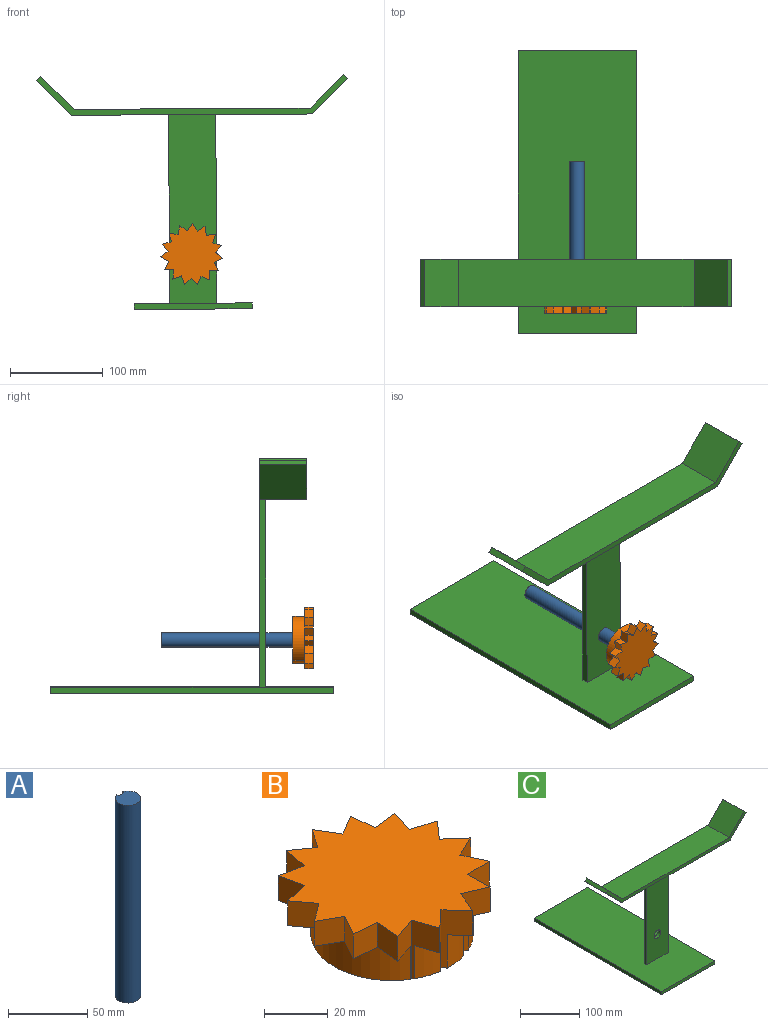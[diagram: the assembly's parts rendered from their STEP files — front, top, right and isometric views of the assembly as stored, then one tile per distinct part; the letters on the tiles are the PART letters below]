
ASSEMBLY  parts=3 mates=2
PART A: 6 faces, bbox 15.9x15.5x152.4 mm
  f0: plane 152.4x4.76mm, normal (0,1,0), area 725.8mm2, adj f1,f3,f4,f5
  f1: plane 152.4x1.59mm, normal (1,0,0), area 241.9mm2, adj f0,f2,f4,f5
  f2: cylinder r=7.94mm len=152.4mm, axis (0,0,-1), area 6863.5mm2, adj f1,f3,f4,f5
  f3: plane 152.4x1.59mm, normal (-1,0,0), area 241.9mm2, adj f0,f2,f4,f5
  f4: plane 15.88x15.51mm, normal (0,0,1), area 189.2mm2, adj f0,f1,f2,f3
  f5: plane 15.88x15.51mm, normal (0,0,-1), area 189.2mm2, adj f0,f1,f2,f3
PART B: 49 faces, bbox 66.6x66.5x22.2 mm
  f0: cylinder r=25.4mm len=50.45mm, axis (0,0,-1), area 1286.4mm2, adj f15,f16,f25,f36
  f1: cylinder r=25.4mm len=12.7mm, axis (0,0,-1), area 117.7mm2, adj f5,f15,f26,f27
  f2: cylinder r=25.4mm len=12.7mm, axis (0,0,-1), area 106.1mm2, adj f6,f15,f28,f29
  f3: cylinder r=25.4mm len=12.7mm, axis (0,0,-1), area 102mm2, adj f7,f15,f30,f31
  f4: cylinder r=25.4mm len=12.7mm, axis (0,0,-1), area 106.1mm2, adj f8,f15,f32,f33
  f5: plane 8.74x8.39mm, normal (0,0,-1), area 29.8mm2, adj f1,f26,f27
  f6: plane 8.25x6.82mm, normal (0,0,-1), area 24.7mm2, adj f2,f28,f29
  f7: plane 7.34x6.74mm, normal (0,0,-1), area 22.9mm2, adj f3,f30,f31
  f8: plane 7.42x7.21mm, normal (0,0,-1), area 24.7mm2, adj f4,f32,f33
  f9: plane 9.2x7.28mm, normal (0,0,-1), area 29.8mm2, adj f14,f34,f35
  f10: plane 12.7x1.59mm, normal (-1,0,0), area 20.2mm2, adj f11,f13,f15,f17
  f11: plane 12.7x4.76mm, normal (0,-1,0), area 60.5mm2, adj f10,f12,f15,f17
  f12: plane 12.7x1.59mm, normal (1,0,0), area 20.2mm2, adj f11,f13,f15,f17
  f13: cylinder r=7.94mm len=15.88mm, axis (0,0,-1), area 572mm2, adj f10,f12,f15,f17
  f14: cylinder r=25.4mm len=12.7mm, axis (0,0,-1), area 117.7mm2, adj f9,f15,f34,f35
  f15: plane 50.8x50.8mm, normal (0,0,-1), area 1826.6mm2, adj f0,f1,f2,f3,f4,f10,f11,f12
  f16: plane 65.64x59.76mm, normal (0,0,-1), area 545.8mm2, adj f0,f18,f19,f20,f21,f22,f23,f24
  f17: plane 15.88x15.51mm, normal (0,0,-1), area 189.2mm2, adj f10,f11,f12,f13
  f18: plane 9.6x9.53mm, normal (-0.22,0.98,0), area 93.8mm2, adj f16,f19,f44,f48
  f19: plane 9.53x7.89mm, normal (-0.8,-0.6,0), area 93.8mm2, adj f16,f18,f20,f48
  f20: plane 9.53x7.89mm, normal (-0.6,0.8,0), area 93.8mm2, adj f16,f19,f21,f48
  f21: plane 9.53x8.59mm, normal (-0.49,-0.87,0), area 93.8mm2, adj f16,f20,f22,f48
  f22: plane 9.53x8.59mm, normal (-0.87,0.49,0), area 93.8mm2, adj f16,f21,f23,f48
  f23: plane 9.8x9.53mm, normal (-0.09,-1,0), area 93.8mm2, adj f16,f22,f24,f48
  f24: plane 9.8x9.53mm, normal (-1,0.09,0), area 93.8mm2, adj f16,f23,f25,f48
  f25: plane 22.23x9.32mm, normal (0.32,-0.95,0), area 104.6mm2, adj f0,f15,f16,f24,f26,f48
  f26: plane 22.23x9.32mm, normal (-0.95,-0.32,0), area 106.4mm2, adj f1,f5,f15,f25,f27,f48
  f27: plane 22.23x7.23mm, normal (0.68,-0.73,0), area 117mm2, adj f1,f5,f15,f26,f28,f48
  f28: plane 22.23x7.23mm, normal (-0.73,-0.68,0), area 119.4mm2, adj f2,f6,f15,f27,f29,f48
  f29: plane 22.23x9.05mm, normal (0.92,-0.39,0), area 124.5mm2, adj f2,f6,f15,f28,f30,f48
  f30: plane 22.23x9.05mm, normal (-0.39,-0.92,0), area 125.6mm2, adj f3,f7,f15,f29,f31,f48
  f31: plane 22.23x9.85mm, normal (1,0.01,0), area 125.6mm2, adj f3,f7,f15,f30,f32,f48
  f32: plane 22.23x9.85mm, normal (0.01,-1,0), area 124.5mm2, adj f4,f8,f15,f31,f33,f48
  f33: plane 22.23x8.94mm, normal (0.91,0.42,0), area 119.4mm2, adj f4,f8,f15,f32,f34,f48
  f34: plane 22.23x8.94mm, normal (0.42,-0.91,0), area 117mm2, adj f9,f14,f15,f33,f35,f48
  f35: plane 22.23x7.4mm, normal (0.66,0.75,0), area 106.4mm2, adj f9,f14,f15,f34,f36,f48
  f36: plane 22.23x7.4mm, normal (0.75,-0.66,0), area 104.6mm2, adj f0,f15,f16,f35,f37,f48
  f37: plane 9.53x9.4mm, normal (0.3,0.96,0), area 93.8mm2, adj f16,f36,f38,f48
  f38: plane 9.53x9.4mm, normal (0.96,-0.3,0), area 93.8mm2, adj f16,f37,f39,f48
  f39: plane 9.78x9.53mm, normal (-0.12,0.99,0), area 93.8mm2, adj f16,f38,f40,f48
  f40: plane 9.78x9.53mm, normal (0.99,0.12,0), area 93.8mm2, adj f16,f39,f41,f48
  f41: plane 9.53x8.46mm, normal (-0.51,0.86,0), area 93.8mm2, adj f16,f40,f42,f48
  f42: plane 9.53x8.46mm, normal (0.86,0.51,0), area 93.8mm2, adj f16,f41,f43,f48
  f43: plane 9.53x8.04mm, normal (-0.82,0.58,0), area 93.8mm2, adj f16,f42,f45,f48
  f44: plane 9.6x9.53mm, normal (-0.98,-0.22,0), area 93.8mm2, adj f16,f18,f47,f48
  f45: plane 9.53x8.04mm, normal (0.58,0.82,0), area 93.8mm2, adj f16,f43,f46,f48
  f46: plane 9.66x9.53mm, normal (-0.98,0.2,0), area 93.8mm2, adj f16,f45,f47,f48
  f47: plane 9.66x9.53mm, normal (0.2,0.98,0), area 93.8mm2, adj f16,f44,f46,f48
  f48: plane 66.55x66.46mm, normal (0,0,1), area 2693.6mm2, adj f18,f19,f20,f21,f22,f23,f24,f25
PART C: 20 faces, bbox 334.8x304.8x251.8 mm
  f0: plane 304.8x127mm, normal (0,0,1), area 38387mm2, adj f1,f2,f3,f4,f6,f7,f8,f9
  f1: plane 127x6.35mm, normal (0,1,0), area 806.5mm2, adj f0,f2,f4,f5
  f2: plane 304.8x6.35mm, normal (-1,0,0), area 1935.5mm2, adj f0,f1,f3,f5
  f3: plane 127x6.35mm, normal (0,-1,0), area 806.5mm2, adj f0,f2,f4,f5
  f4: plane 304.8x6.35mm, normal (1,0,0), area 1935.5mm2, adj f0,f1,f3,f5
  f5: plane 304.8x127mm, normal (0,0,-1), area 38709.6mm2, adj f1,f2,f3,f4
  f6: plane 334.82x245.47mm, normal (0,1,0), area 12416.1mm2, adj f0,f7,f9,f10,f11,f12,f13,f14
  f7: plane 203.2x6.35mm, normal (-1,0,0), area 1290.3mm2, adj f0,f6,f8,f11
  f8: plane 203.2x50.8mm, normal (0,-1,0), area 10124.6mm2, adj f0,f7,f9,f10,f11
  f9: plane 203.2x6.35mm, normal (1,0,0), area 1290.3mm2, adj f0,f6,f8,f11
  f10: cylinder r=7.94mm len=15.88mm, axis (0,-1,0), area 316.7mm2, adj f6,f8
  f11: plane 259.26x50.8mm, normal (0,0,-1), area 12847.9mm2, adj f6,f7,f8,f9,f12,f18,f19
  f12: plane 50.8x37.78mm, normal (-0.71,0,-0.71), area 2714.3mm2, adj f6,f11,f13,f19
  f13: plane 50.8x4.49mm, normal (-0.71,0,0.71), area 322.6mm2, adj f6,f12,f14,f19
  f14: plane 50.8x35.92mm, normal (0.71,0,0.71), area 2580.6mm2, adj f6,f13,f15,f19
  f15: plane 254x50.8mm, normal (0,0,1), area 12903.2mm2, adj f6,f14,f16,f19
  f16: plane 50.8x35.92mm, normal (-0.71,0,0.71), area 2580.6mm2, adj f6,f15,f17,f19
  f17: plane 50.8x4.49mm, normal (0.71,0,0.71), area 322.6mm2, adj f6,f16,f18,f19
  f18: plane 50.8x37.78mm, normal (0.71,0,-0.71), area 2714.3mm2, adj f6,f11,f17,f19
  f19: plane 334.82x42.27mm, normal (0,-1,0), area 2291.5mm2, adj f11,f12,f13,f14,f15,f16,f17,f18
PLACE A rot(axis=(-0.98,0.13,0.13),91deg) t=(-19.15,32.01,51.47)mm
PLACE B rot(axis=(1,-0.01,0.01),90deg) t=(-19.15,30.39,51.47)mm
PLACE C rot(axis=(0,-1,0),0.3deg) t=(-18.88,75.52,0.67)mm fixed
MATE cylindrical A.f2 <-> C.f10  axis (0,-1,0) through (-19.15,32.01,51.47)mm
MATE cylindrical B.f0 <-> A.f2  axis (0,1,0) through (-19.15,-39.46,51.47)mm
